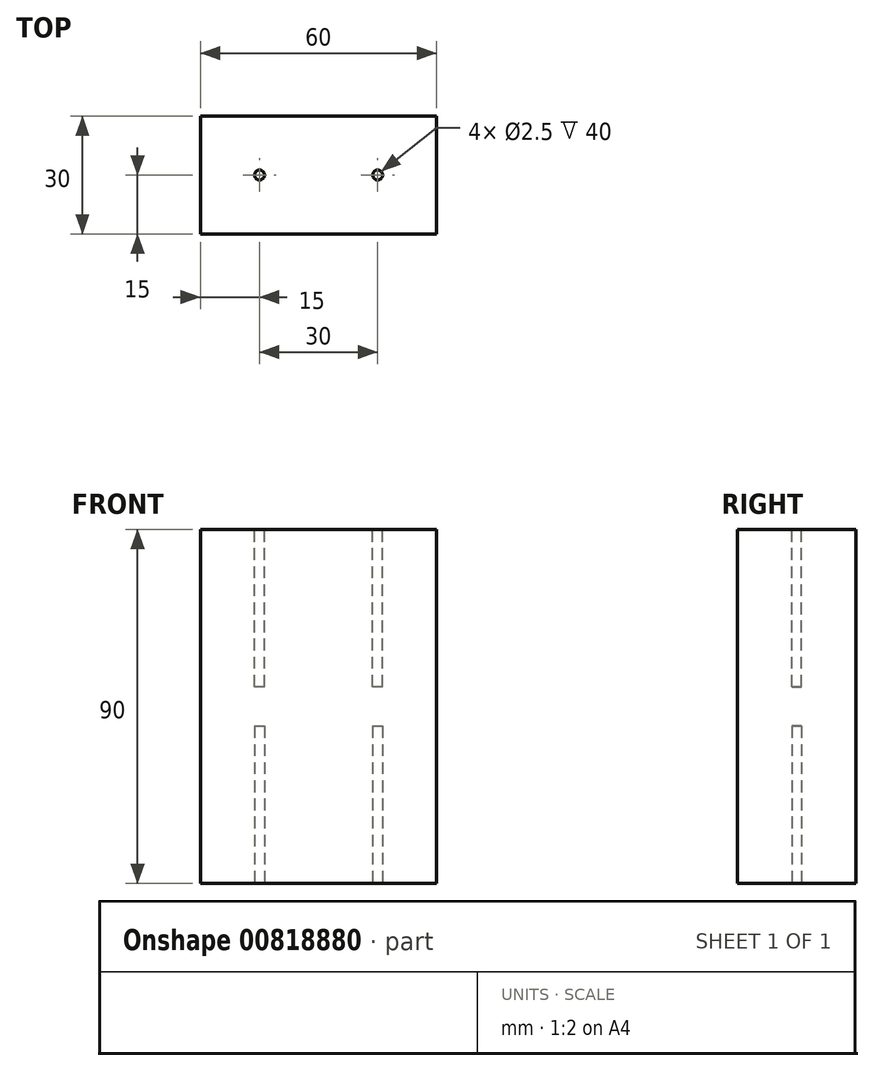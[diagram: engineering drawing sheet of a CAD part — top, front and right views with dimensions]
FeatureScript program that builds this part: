
annotation { "Feature Type Name" : "Feature", "Feature Type Description" : "" }
export const myFeature = defineFeature(function(context is Context, id is Id, definition is map)
    precondition{}
    {
        {
            var Q0;
            Q0=qCreatedBy(makeId("Top.planeOp"),FACE);
            var sketch = newSketch(context, id + "F0", { "sketchPlane" : qUnion([Q0])});
            skLineSegment(sketch, "E0.bottom", {"start": v(-30, 15) * mm, "end": v(30, 15) * mm});
            skLineSegment(sketch, "E0.top", {"start": v(-30, -15) * mm, "end": v(30, -15) * mm});
            skLineSegment(sketch, "E0.left", {"start": v(-30, 15) * mm, "end": v(-30, -15) * mm});
            skLineSegment(sketch, "E0.right", {"start": v(30, 15) * mm, "end": v(30, -15) * mm});
            skPoint(sketch, "E0.middle", {"position": v(0, 0) * mm});
            skSolve(sketch);
        }
        {
            var Q0;
            Q0=makeQuery(id+"F0.imprint","IMPRINT",FACE,{"disambiguationData":[TD([[makeQuery(id+"F0.imprint","IMPRINT",EDGE,{"derivedFrom":sQuery(id+"F0.wireOp",EDGE,"E0.bottom")}),-1.0]])]});
            extrude(context, id + "F1", {"entities" : qUnion([Q0]), "depth" : 90 * mm, "offsetDistance" : 25 * mm});
        }
        {
            var Q0;
            Q0=makeQuery(id+"F1.opExtrude","CAP_FACE",FACE,{"disambiguationData":[OSD([sQuery(id+"F0.wireOp",EDGE,"E0.bottom"),sQuery(id+"F0.wireOp",EDGE,"E0.top"),sQuery(id+"F0.wireOp",EDGE,"E0.left"),sQuery(id+"F0.wireOp",EDGE,"E0.right")])],"isStart":true});
            var sketch = newSketch(context, id + "F2", { "sketchPlane" : qUnion([Q0])});
            skCircle(sketch, "E1", {"center": v(0, 0) * mm, "radius": 2.5 * mm});
            skSolve(sketch);
        }
        {
            var Q0;
            Q0=makeQuery(id+"F1.opExtrude","CAP_FACE",FACE,{"disambiguationData":[OSD([sQuery(id+"F0.wireOp",EDGE,"E0.bottom"),sQuery(id+"F0.wireOp",EDGE,"E0.top"),sQuery(id+"F0.wireOp",EDGE,"E0.left"),sQuery(id+"F0.wireOp",EDGE,"E0.right")])],"isStart":false});
            var sketch = newSketch(context, id + "F3", { "sketchPlane" : qUnion([Q0])});
            skCircle(sketch, "E2", {"center": v(-15, 0) * mm, "radius": 1.25 * mm});
            skCircle(sketch, "E3", {"center": v(15, 0) * mm, "radius": 1.25 * mm});
            skSolve(sketch);
        }
        {
            var Q0;
            Q0=makeQuery(id+"F3.imprint","IMPRINT",FACE,{"disambiguationData":[TD([[makeQuery(id+"F3.imprint","IMPRINT",EDGE,{"derivedFrom":sQuery(id+"F3.wireOp",EDGE,"E2")}),1.0]])]});
            var Q1;
            Q1=makeQuery(id+"F3.imprint","IMPRINT",FACE,{"disambiguationData":[TD([[makeQuery(id+"F3.imprint","IMPRINT",EDGE,{"derivedFrom":sQuery(id+"F3.wireOp",EDGE,"E3")}),1.0]])]});
            extrude(context, id + "F4", {"entities" : qUnion([Q0, Q1]), "operationType" : NewBodyOperationType.REMOVE, "oppositeDirection" : true, "depth" : 40 * mm, "offsetDistance" : 25 * mm});
        }
        {
            var Q0;
            Q0=makeQuery(id+"F2.imprint","IMPRINT",FACE,{"disambiguationData":[TD([[makeQuery(id+"F2.imprint","IMPRINT",EDGE,{"derivedFrom":sQuery(id+"F2.wireOp",EDGE,"E1")}),-1.0]])]});
            var sketch = newSketch(context, id + "F5", { "sketchPlane" : qUnion([Q0])});
            skCircle(sketch, "E4", {"center": v(-15, 0) * mm, "radius": 1.25 * mm});
            skCircle(sketch, "E5", {"center": v(15, 0) * mm, "radius": 1.25 * mm});
            skSolve(sketch);
        }
        {
            var Q0;
            Q0 = qSketchRegion(id + "F5", true);
            extrude(context, id + "F6", {"entities" : qUnion([Q0]), "operationType" : NewBodyOperationType.REMOVE, "oppositeDirection" : true, "depth" : 40 * mm, "offsetDistance" : 25 * mm});
        }
    });
